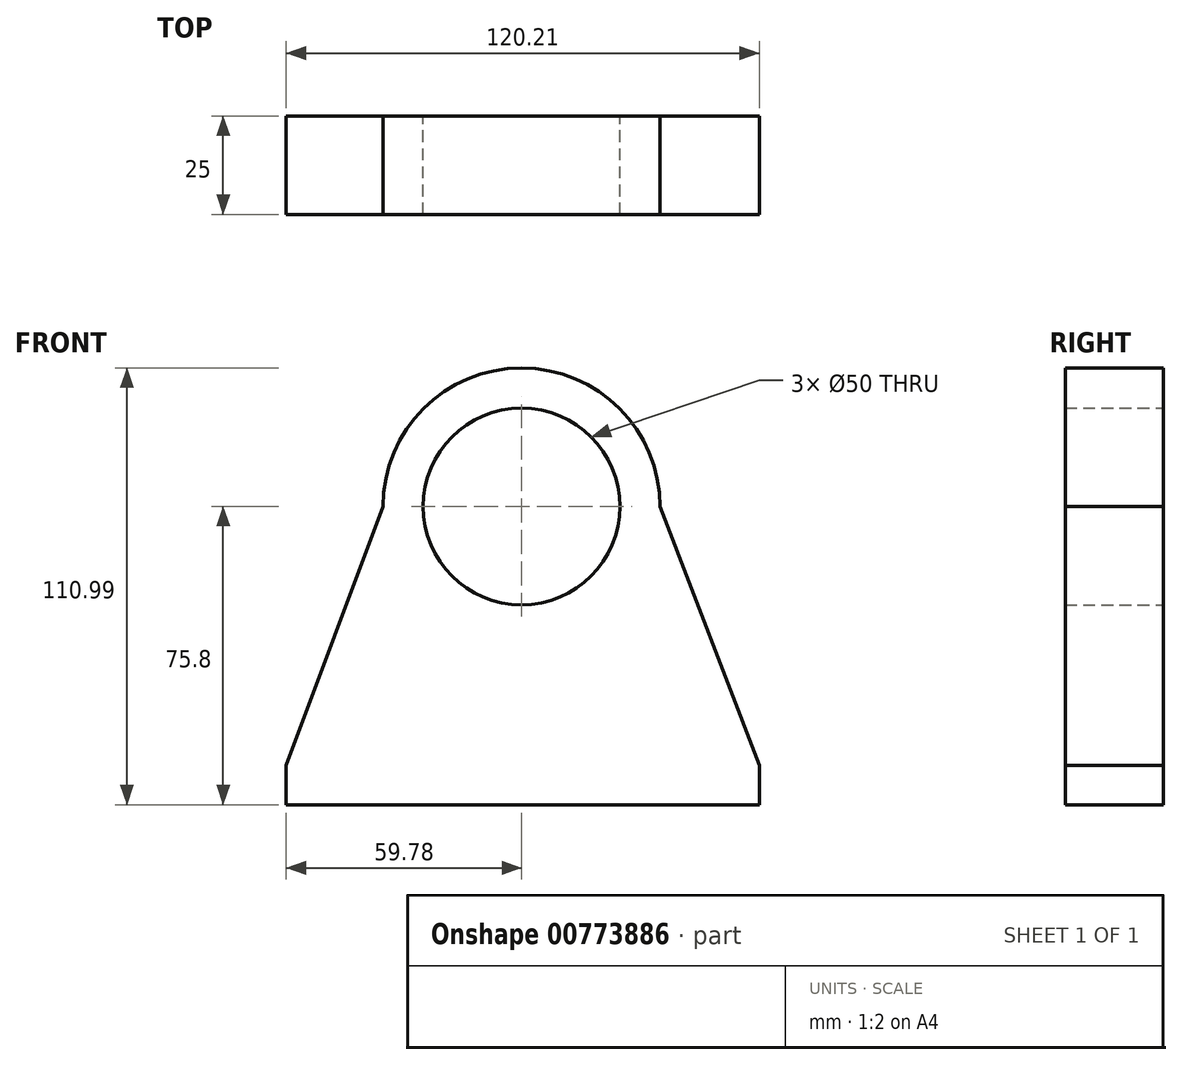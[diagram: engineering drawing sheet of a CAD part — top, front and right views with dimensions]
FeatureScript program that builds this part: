
annotation { "Feature Type Name" : "Feature", "Feature Type Description" : "" }
export const myFeature = defineFeature(function(context is Context, id is Id, definition is map)
    precondition{}
    {
        {
            var Q0;
            Q0=qCreatedBy(makeId("Front.planeOp"),FACE);
            var sketch = newSketch(context, id + "F0", { "sketchPlane" : qUnion([Q0])});
            skCircle(sketch, "E0", {"center": v(0, 0) * mm, "radius": 35.2 * mm});
            skCircle(sketch, "E1", {"center": v(0, 0) * mm, "radius": 25 * mm});
            skLineSegment(sketch, "E2.bottom", {"start": v(-59.78, -65.8) * mm, "end": v(60.43, -65.8) * mm});
            skLineSegment(sketch, "E2.top", {"start": v(-59.78, -75.8) * mm, "end": v(60.43, -75.8) * mm});
            skLineSegment(sketch, "E2.left", {"start": v(-59.78, -65.8) * mm, "end": v(-59.78, -75.8) * mm});
            skLineSegment(sketch, "E2.right", {"start": v(60.43, -65.8) * mm, "end": v(60.43, -75.8) * mm});
            skLineSegment(sketch, "E3", {"start": v(-35.2, 0) * mm, "end": v(-59.78, -65.8) * mm});
            skLineSegment(sketch, "E4", {"start": v(35.2, 0) * mm, "end": v(60.43, -65.8) * mm});
            skSolve(sketch);
        }
        {
            var Q0;
            Q0 = qSketchRegion(id + "F0", true);
            extrude(context, id + "F1", {"entities" : qUnion([Q0]), "depth" : 25 * mm, "offsetDistance" : 25 * mm});
        }
    });
